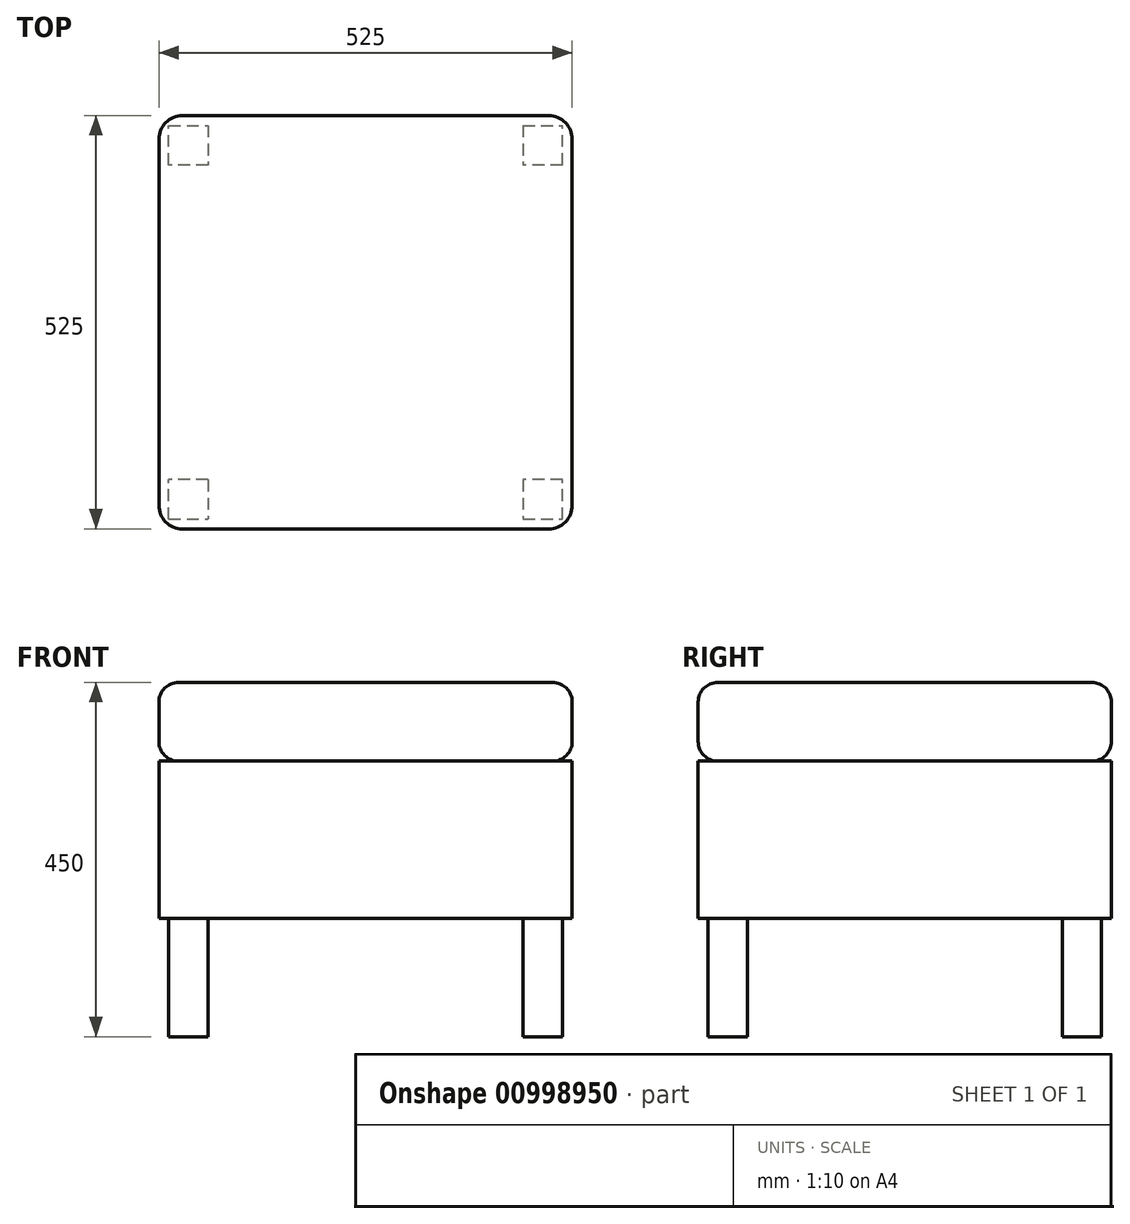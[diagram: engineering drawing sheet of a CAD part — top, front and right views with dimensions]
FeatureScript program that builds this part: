
annotation { "Feature Type Name" : "Feature", "Feature Type Description" : "" }
export const myFeature = defineFeature(function(context is Context, id is Id, definition is map)
    precondition{}
    {
        {
            var Q0;
            Q0=qCreatedBy(makeId("Top.planeOp"),FACE);
            var sketch = newSketch(context, id + "F0", { "sketchPlane" : qUnion([Q0])});
            skLineSegment(sketch, "E0.bottom", {"start": v(-250, -250) * mm, "end": v(250, -250) * mm});
            skLineSegment(sketch, "E0.top", {"start": v(-250, 250) * mm, "end": v(250, 250) * mm});
            skLineSegment(sketch, "E0.left", {"start": v(-250, -250) * mm, "end": v(-250, 250) * mm});
            skLineSegment(sketch, "E0.right", {"start": v(250, -250) * mm, "end": v(250, 250) * mm});
            skPoint(sketch, "E0.middle", {"position": v(0, 0) * mm});
            skSolve(sketch);
        }
        {
            var Q0;
            Q0=makeQuery(id+"F0.imprint","IMPRINT",FACE,{"disambiguationData":[TD([[makeQuery(id+"F0.imprint","IMPRINT",EDGE,{"derivedFrom":sQuery(id+"F0.wireOp",EDGE,"E0.bottom")}),1.0]])]});
            extrude(context, id + "F1", {"entities" : qUnion([Q0]), "oppositeDirection" : true, "depth" : 150 * mm, "offsetDistance" : 25 * mm});
        }
        {
            var Q0;
            Q0=makeQuery(id+"F1.opExtrude","SWEPT_FACE",FACE,{"disambiguationData":[OSD([sQuery(id+"F0.wireOp",EDGE,"E0.bottom")])]});
            var sketch = newSketch(context, id + "F2", { "sketchPlane" : qUnion([Q0])});
            skLineSegment(sketch, "E1.bottom", {"start": v(-200, -150) * mm, "end": v(200, -150) * mm});
            skLineSegment(sketch, "E1.top", {"start": v(-200, 0) * mm, "end": v(200, 0) * mm});
            skLineSegment(sketch, "E1.left", {"start": v(-200, -150) * mm, "end": v(-200, 0) * mm});
            skLineSegment(sketch, "E1.right", {"start": v(200, -150) * mm, "end": v(200, 0) * mm});
            skSolve(sketch);
        }
        {
            var Q0;
            Q0=makeQuery(id+"F2.imprint","IMPRINT",FACE,{"disambiguationData":[TD([[makeQuery(id+"F2.imprint","IMPRINT",EDGE,{"derivedFrom":sQuery(id+"F2.wireOp",EDGE,"E1.bottom")}),1.0]])]});
            extrude(context, id + "F3", {"entities" : qUnion([Q0]), "operationType" : NewBodyOperationType.REMOVE, "endBound" : BoundingType.THROUGH_ALL, "oppositeDirection" : true, "depth" : 25 * mm, "offsetDistance" : 25 * mm});
        }
        {
            var Q0;
            Q0=makeQuery(id+"F1.opExtrude","SWEPT_FACE",FACE,{"disambiguationData":[OSD([sQuery(id+"F0.wireOp",EDGE,"E0.left")])]});
            var sketch = newSketch(context, id + "F4", { "sketchPlane" : qUnion([Q0])});
            skLineSegment(sketch, "E2.bottom", {"start": v(-200, -150) * mm, "end": v(200, -150) * mm});
            skLineSegment(sketch, "E2.top", {"start": v(-200, 0) * mm, "end": v(200, 0) * mm});
            skLineSegment(sketch, "E2.left", {"start": v(-200, -150) * mm, "end": v(-200, 0) * mm});
            skLineSegment(sketch, "E2.right", {"start": v(200, -150) * mm, "end": v(200, 0) * mm});
            skSolve(sketch);
        }
        {
            var Q0;
            Q0=makeQuery(id+"F4.imprint","IMPRINT",FACE,{"disambiguationData":[TD([[makeQuery(id+"F4.imprint","IMPRINT",EDGE,{"derivedFrom":sQuery(id+"F4.wireOp",EDGE,"E2.bottom")}),-1.0]])]});
            extrude(context, id + "F5", {"entities" : qUnion([Q0]), "operationType" : NewBodyOperationType.REMOVE, "endBound" : BoundingType.THROUGH_ALL, "oppositeDirection" : true, "depth" : 25 * mm, "offsetDistance" : 25 * mm});
        }
        {
            var Q0;
            Q0=makeQuery(id+"F1.opExtrude","SWEPT_FACE",FACE,{"disambiguationData":[OSD([sQuery(id+"F0.wireOp",EDGE,"E0.right")])]});
            var sketch = newSketch(context, id + "F6", { "sketchPlane" : qUnion([Q0])});
            skLineSegment(sketch, "E3.bottom", {"start": v(-200, -150) * mm, "end": v(200, -150) * mm});
            skLineSegment(sketch, "E3.top", {"start": v(-200, 0) * mm, "end": v(200, 0) * mm});
            skLineSegment(sketch, "E3.left", {"start": v(-200, -150) * mm, "end": v(-200, 0) * mm});
            skLineSegment(sketch, "E3.right", {"start": v(200, -150) * mm, "end": v(200, 0) * mm});
            skSolve(sketch);
        }
        {
            var Q0;
            Q0=makeQuery(id+"F6.imprint","IMPRINT",FACE,{"disambiguationData":[TD([[makeQuery(id+"F6.imprint","IMPRINT",EDGE,{"derivedFrom":sQuery(id+"F6.wireOp",EDGE,"E3.bottom")}),1.0]])]});
            extrude(context, id + "F7", {"entities" : qUnion([Q0]), "operationType" : NewBodyOperationType.REMOVE, "endBound" : BoundingType.THROUGH_ALL, "oppositeDirection" : true, "depth" : 25 * mm, "offsetDistance" : 25 * mm});
        }
        {
            var Q0;
            Q0=qCreatedBy(makeId("Top.planeOp"),FACE);
            var sketch = newSketch(context, id + "F8", { "sketchPlane" : qUnion([Q0])});
            skLineSegment(sketch, "E4.bottom", {"start": v(-262.5, -262.5) * mm, "end": v(262.5, -262.5) * mm});
            skLineSegment(sketch, "E4.top", {"start": v(-262.5, 262.5) * mm, "end": v(262.5, 262.5) * mm});
            skLineSegment(sketch, "E4.left", {"start": v(-262.5, -262.5) * mm, "end": v(-262.5, 262.5) * mm});
            skLineSegment(sketch, "E4.right", {"start": v(262.5, -262.5) * mm, "end": v(262.5, 262.5) * mm});
            skPoint(sketch, "E4.middle", {"position": v(0, 0) * mm});
            skSolve(sketch);
        }
        {
            var Q0;
            Q0 = qSketchRegion(id + "F8", true);
            extrude(context, id + "F9", {"entities" : qUnion([Q0]), "depth" : 200 * mm, "offsetDistance" : 25 * mm});
        }
        {
            var Q0;
            Q0=makeQuery(id+"F9.opExtrude","CAP_FACE",FACE,{"disambiguationData":[OSD([sQuery(id+"F8.wireOp",EDGE,"E4.bottom"),sQuery(id+"F8.wireOp",EDGE,"E4.top"),sQuery(id+"F8.wireOp",EDGE,"E4.left"),sQuery(id+"F8.wireOp",EDGE,"E4.right")])],"isStart":false});
            var sketch = newSketch(context, id + "F10", { "sketchPlane" : qUnion([Q0])});
            skLineSegment(sketch, "E5.bottom", {"start": v(262.5, -262.5) * mm, "end": v(-262.5, -262.5) * mm});
            skLineSegment(sketch, "E5.top", {"start": v(262.5, 262.5) * mm, "end": v(-262.5, 262.5) * mm});
            skLineSegment(sketch, "E5.left", {"start": v(262.5, -262.5) * mm, "end": v(262.5, 262.5) * mm});
            skLineSegment(sketch, "E5.right", {"start": v(-262.5, -262.5) * mm, "end": v(-262.5, 262.5) * mm});
            skPoint(sketch, "E5.middle", {"position": v(0, 0) * mm});
            skSolve(sketch);
        }
        {
            var Q0;
            Q0=makeQuery(id+"F10.imprint","IMPRINT",FACE,{"disambiguationData":[TD([[makeQuery(id+"F10.imprint","IMPRINT",EDGE,{"derivedFrom":sQuery(id+"F10.wireOp",EDGE,"E5.bottom")}),1.0]])]});
            var sketch = newSketch(context, id + "F11", { "sketchPlane" : qUnion([Q0])});
            skLineSegment(sketch, "E6.bottom", {"start": v(-262.5, 262.5) * mm, "end": v(262.5, 262.5) * mm});
            skLineSegment(sketch, "E6.top", {"start": v(-262.5, -262.5) * mm, "end": v(262.5, -262.5) * mm});
            skLineSegment(sketch, "E6.left", {"start": v(-262.5, 262.5) * mm, "end": v(-262.5, -262.5) * mm});
            skLineSegment(sketch, "E6.right", {"start": v(262.5, 262.5) * mm, "end": v(262.5, -262.5) * mm});
            skPoint(sketch, "E6.middle", {"position": v(0, 0) * mm});
            skSolve(sketch);
        }
        {
            var Q0;
            Q0 = qSketchRegion(id + "F11", true);
            extrude(context, id + "F12", {"entities" : qUnion([Q0]), "depth" : 100 * mm, "offsetDistance" : 25 * mm});
        }
        {
            var Q0;
            Q0=makeQuery(id+"F12.opExtrude","CAP_EDGE",EDGE,{"disambiguationData":[OSD([sQuery(id+"F11.wireOp",EDGE,"E6.bottom")])],"isStart":true});
            var Q1;
            Q1=makeQuery(id+"F12.opExtrude","CAP_EDGE",EDGE,{"disambiguationData":[OSD([sQuery(id+"F11.wireOp",EDGE,"E6.right")])],"isStart":true});
            var Q2;
            Q2=makeQuery(id+"F12.opExtrude","CAP_EDGE",EDGE,{"disambiguationData":[OSD([sQuery(id+"F11.wireOp",EDGE,"E6.left")])],"isStart":true});
            var Q3;
            Q3=makeQuery(id+"F12.opExtrude","CAP_EDGE",EDGE,{"disambiguationData":[OSD([sQuery(id+"F11.wireOp",EDGE,"E6.top")])],"isStart":true});
            fillet(context, id + "F13", {"entities" : qUnion([Q0, Q1, Q2, Q3]), "radius" : 25 * mm, "tangentPropagation" : true, "allowEdgeOverflow" : false});
        }
        {
            var Q0;
            Q0=makeQuery(id+"F12.opExtrude","CAP_EDGE",EDGE,{"disambiguationData":[OSD([sQuery(id+"F11.wireOp",EDGE,"E6.bottom")])],"isStart":false});
            var Q1;
            Q1=makeQuery(id+"F12.opExtrude","CAP_EDGE",EDGE,{"disambiguationData":[OSD([sQuery(id+"F11.wireOp",EDGE,"E6.right")])],"isStart":false});
            var Q2;
            Q2=makeQuery(id+"F12.opExtrude","CAP_EDGE",EDGE,{"disambiguationData":[OSD([sQuery(id+"F11.wireOp",EDGE,"E6.left")])],"isStart":false});
            var Q3;
            Q3=makeQuery(id+"F12.opExtrude","CAP_EDGE",EDGE,{"disambiguationData":[OSD([sQuery(id+"F11.wireOp",EDGE,"E6.top")])],"isStart":false});
            fillet(context, id + "F14", {"entities" : qUnion([Q0, Q1, Q2, Q3]), "radius" : 25 * mm, "tangentPropagation" : true, "allowEdgeOverflow" : false});
        }
        {
            var Q0;
            Q0=makeQuery(id+"F12.opExtrude","SWEPT_EDGE",EDGE,{"disambiguationData":[OSD([sQuery(id+"F11.wireOp",EDGE,"E6.bottom"),sQuery(id+"F11.wireOp",EDGE,"E6.left")])]});
            var Q1;
            Q1=makeQuery(id+"F9.opExtrude","SWEPT_EDGE",EDGE,{"disambiguationData":[OSD([sQuery(id+"F8.wireOp",EDGE,"E4.top"),sQuery(id+"F8.wireOp",EDGE,"E4.left")])]});
            var Q2;
            Q2=makeQuery(id+"F9.opExtrude","SWEPT_EDGE",EDGE,{"disambiguationData":[OSD([sQuery(id+"F8.wireOp",EDGE,"E4.top"),sQuery(id+"F8.wireOp",EDGE,"E4.right")])]});
            var Q3;
            Q3=makeQuery(id+"F12.opExtrude","SWEPT_EDGE",EDGE,{"disambiguationData":[OSD([sQuery(id+"F11.wireOp",EDGE,"E6.bottom"),sQuery(id+"F11.wireOp",EDGE,"E6.right")])]});
            var Q4;
            Q4=makeQuery(id+"F9.opExtrude","SWEPT_EDGE",EDGE,{"disambiguationData":[OSD([sQuery(id+"F8.wireOp",EDGE,"E4.bottom"),sQuery(id+"F8.wireOp",EDGE,"E4.right")])]});
            var Q5;
            Q5=makeQuery(id+"F12.opExtrude","SWEPT_EDGE",EDGE,{"disambiguationData":[OSD([sQuery(id+"F11.wireOp",EDGE,"E6.top"),sQuery(id+"F11.wireOp",EDGE,"E6.right")])]});
            var Q6;
            Q6=makeQuery(id+"F12.opExtrude","SWEPT_EDGE",EDGE,{"disambiguationData":[OSD([sQuery(id+"F11.wireOp",EDGE,"E6.top"),sQuery(id+"F11.wireOp",EDGE,"E6.left")])]});
            var Q7;
            Q7=makeQuery(id+"F9.opExtrude","SWEPT_EDGE",EDGE,{"disambiguationData":[OSD([sQuery(id+"F8.wireOp",EDGE,"E4.bottom"),sQuery(id+"F8.wireOp",EDGE,"E4.left")])]});
            fillet(context, id + "F15", {"entities" : qUnion([Q0, Q1, Q2, Q3, Q4, Q5, Q6, Q7]), "radius" : 30 * mm, "tangentPropagation" : true, "allowEdgeOverflow" : false});
        }
    });
